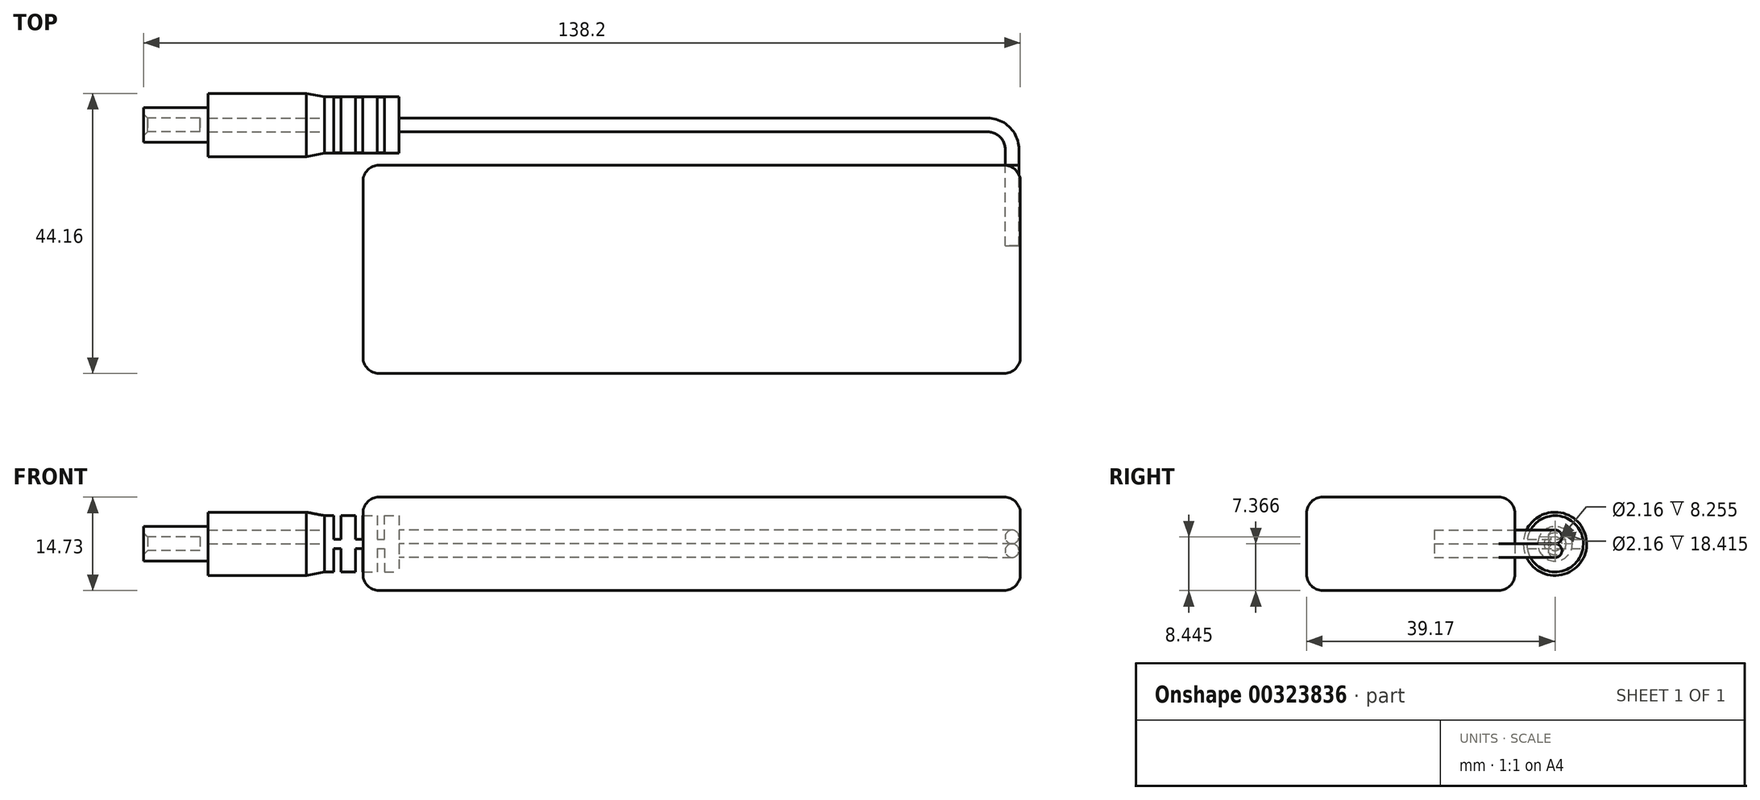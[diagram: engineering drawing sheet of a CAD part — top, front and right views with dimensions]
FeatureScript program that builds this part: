
annotation { "Feature Type Name" : "Feature", "Feature Type Description" : "" }
export const myFeature = defineFeature(function(context is Context, id is Id, definition is map)
    precondition{}
    {
        {
            var Q0;
            Q0=qCreatedBy(makeId("Top.planeOp"),FACE);
            var sketch = newSketch(context, id + "F0", { "sketchPlane" : qUnion([Q0])});
            skLineSegment(sketch, "E0.bottom", {"start": v(0, 0) * mm, "end": v(103.62, 0) * mm});
            skLineSegment(sketch, "E0.top", {"start": v(0, -32.82) * mm, "end": v(103.62, -32.82) * mm});
            skLineSegment(sketch, "E0.left", {"start": v(0, 0) * mm, "end": v(0, -32.82) * mm});
            skLineSegment(sketch, "E0.right", {"start": v(103.62, 0) * mm, "end": v(103.62, -32.82) * mm});
            skSolve(sketch);
        }
        {
            var Q0;
            Q0=makeQuery(id+"F0.imprint","IMPRINT",FACE,{"disambiguationData":[TD([[makeQuery(id+"F0.imprint","IMPRINT",EDGE,{"derivedFrom":sQuery(id+"F0.wireOp",EDGE,"E0.bottom")}),-1.0]])]});
            extrude(context, id + "F1", {"entities" : qUnion([Q0]), "depth" : 14.73 * mm});
        }
        {
            var Q0;
            Q0=makeQuery(id+"F1.opExtrude","CAP_EDGE",EDGE,{"disambiguationData":[OSD([sQuery(id+"F0.wireOp",EDGE,"E0.top")])],"isStart":false});
            var Q1;
            Q1=makeQuery(id+"F1.opExtrude","CAP_FACE",FACE,{"disambiguationData":[OSD([sQuery(id+"F0.wireOp",EDGE,"E0.bottom"),sQuery(id+"F0.wireOp",EDGE,"E0.top"),sQuery(id+"F0.wireOp",EDGE,"E0.left"),sQuery(id+"F0.wireOp",EDGE,"E0.right")])],"isStart":false});
            var Q2;
            Q2=makeQuery(id+"F1.opExtrude","SWEPT_EDGE",EDGE,{"disambiguationData":[OSD([sQuery(id+"F0.wireOp",EDGE,"E0.top"),sQuery(id+"F0.wireOp",EDGE,"E0.right")])]});
            var Q3;
            Q3=makeQuery(id+"F1.opExtrude","SWEPT_EDGE",EDGE,{"disambiguationData":[OSD([sQuery(id+"F0.wireOp",EDGE,"E0.bottom"),sQuery(id+"F0.wireOp",EDGE,"E0.right")])]});
            var Q4;
            Q4=makeQuery(id+"F1.opExtrude","CAP_EDGE",EDGE,{"disambiguationData":[OSD([sQuery(id+"F0.wireOp",EDGE,"E0.right")])],"isStart":true});
            var Q5;
            Q5=makeQuery(id+"F1.opExtrude","CAP_FACE",FACE,{"disambiguationData":[OSD([sQuery(id+"F0.wireOp",EDGE,"E0.bottom"),sQuery(id+"F0.wireOp",EDGE,"E0.top"),sQuery(id+"F0.wireOp",EDGE,"E0.left"),sQuery(id+"F0.wireOp",EDGE,"E0.right")])],"isStart":true});
            var Q6;
            Q6=makeQuery(id+"F1.opExtrude","SWEPT_FACE",FACE,{"disambiguationData":[OSD([sQuery(id+"F0.wireOp",EDGE,"E0.left")])]});
            var Q7;
            Q7=makeQuery(id+"F1.opExtrude","SWEPT_FACE",FACE,{"disambiguationData":[OSD([sQuery(id+"F0.wireOp",EDGE,"E0.top")])]});
            fillet(context, id + "F2", {"entities" : qUnion([Q0, Q1, Q2, Q3, Q4, Q5, Q6, Q7]), "radius" : 2.54 * mm, "tangentPropagation" : true, "allowEdgeOverflow" : false});
        }
        {
            var Q0;
            Q0=makeQuery(id+"F1.opExtrude","SWEPT_FACE",FACE,{"disambiguationData":[OSD([sQuery(id+"F0.wireOp",EDGE,"E0.bottom")])]});
            var sketch = newSketch(context, id + "F3", { "sketchPlane" : qUnion([Q0])});
            skCircle(sketch, "E1", {"center": v(-102.3, 6.29) * mm, "radius": 1.08 * mm});
            skCircle(sketch, "E2", {"center": v(-102.3, 8.45) * mm, "radius": 1.08 * mm});
            skSolve(sketch);
        }
        {
            var Q0;
            Q0=makeQuery(id+"F3.imprint","IMPRINT",FACE,{"disambiguationData":[TD([[makeQuery(id+"F3.imprint","IMPRINT",EDGE,{"derivedFrom":sQuery(id+"F3.wireOp",EDGE,"E1")}),1.0]])]});
            var Q1;
            Q1=makeQuery(id+"F3.imprint","IMPRINT",FACE,{"disambiguationData":[TD([[makeQuery(id+"F3.imprint","IMPRINT",EDGE,{"derivedFrom":sQuery(id+"F3.wireOp",EDGE,"E2")}),1.0]])]});
            extrude(context, id + "F4", {"entities" : qUnion([Q0, Q1]), "oppositeDirection" : true, "depth" : 12.7 * mm});
        }
        {
            var Q0;
            Q0=makeQuery(id+"F1.opExtrude","CAP_FACE",FACE,{"disambiguationData":[OSD([sQuery(id+"F0.wireOp",EDGE,"E0.bottom"),sQuery(id+"F0.wireOp",EDGE,"E0.top"),sQuery(id+"F0.wireOp",EDGE,"E0.left"),sQuery(id+"F0.wireOp",EDGE,"E0.right")])],"isStart":true});
            cPlane(context, id + "F5", {"entities" : qUnion([Q0]), "cplaneType" : CPlaneType.OFFSET, "offset" : 6.25 * mm, "oppositeDirection" : true, "width" : 152.4 * mm, "height" : 152.4 * mm});
        }
        {
            var Q0;
            Q0=qCreatedBy(id+"F5.planeOp",FACE);
            cPlane(context, id + "F6", {"entities" : qUnion([Q0]), "cplaneType" : CPlaneType.OFFSET, "offset" : 2.18 * mm, "oppositeDirection" : true, "width" : 152.4 * mm, "height" : 152.4 * mm});
        }
        {
            var Q0;
            Q0=qCreatedBy(id+"F5.planeOp",FACE);
            var sketch = newSketch(context, id + "F7", { "sketchPlane" : qUnion([Q0])});
            skPoint(sketch, "E3.endSnap0", {"position": v(102.3, 0) * mm});
            skLineSegment(sketch, "E4", {"start": v(102.3, 0) * mm, "end": v(102.3, -2.54) * mm});
            skLineSegment(sketch, "E5", {"start": v(98.5, -6.35) * mm, "end": v(5.66, -6.35) * mm});
            skPoint(sketch, "E6.visualSharp", {"position": v(102.3, -6.35) * mm});
            skArc(sketch, "E6.filletArc", {"start": v(98.5, -6.35) * mm, "mid": v(101.2, -5.23) * mm, "end": v(102.3, -2.54) * mm});
            skSolve(sketch);
        }
        {
            var Q0;
            Q0=qCreatedBy(id+"F6.planeOp",FACE);
            var sketch = newSketch(context, id + "F8", { "sketchPlane" : qUnion([Q0])});
            skLineSegment(sketch, "E7.0", {"start": v(102.3, 0) * mm, "end": v(102.3, -2.54) * mm});
            skArc(sketch, "E8.0", {"start": v(98.5, -6.35) * mm, "mid": v(101.2, -5.23) * mm, "end": v(102.3, -2.54) * mm});
            skLineSegment(sketch, "E9.0", {"start": v(98.5, -6.35) * mm, "end": v(5.66, -6.35) * mm});
            skSolve(sketch);
        }
        {
            var Q0;
            Q0=makeQuery(id+"F4.opExtrude","CAP_FACE",FACE,{"disambiguationData":[OSD([sQuery(id+"F3.wireOp",EDGE,"E1")])],"isStart":true});
            var Q1;
            Q1=sQuery(id+"F7.wireOp",EDGE,"E4");
            var Q2;
            Q2=sQuery(id+"F7.wireOp",EDGE,"E6.filletArc");
            var Q3;
            Q3=sQuery(id+"F7.wireOp",EDGE,"E5");
            sweep(context, id + "F9", {"operationType" : NewBodyOperationType.ADD, "profiles" : qUnion([Q0]), "path" : qUnion([Q1, Q2, Q3])});
        }
        {
            var Q0;
            Q0=makeQuery(id+"F4.opExtrude","CAP_FACE",FACE,{"disambiguationData":[OSD([sQuery(id+"F3.wireOp",EDGE,"E2")])],"isStart":true});
            var Q1;
            Q1=sQuery(id+"F8.wireOp",EDGE,"E7.0");
            var Q2;
            Q2=sQuery(id+"F8.wireOp",EDGE,"E8.0");
            var Q3;
            Q3=sQuery(id+"F8.wireOp",EDGE,"E9.0");
            sweep(context, id + "F10", {"profiles" : qUnion([Q0]), "path" : qUnion([Q1, Q2, Q3])});
        }
        {
            var Q0;
            Q0=makeQuery(id+"F10.opSweep","CAP_FACE",FACE,{"disambiguationData":[OSD([sQuery(id+"F3.wireOp",EDGE,"E2"),sQuery(id+"F8.wireOp",VERTEX,"E9.0.end")])],"isStart":false});
            var sketch = newSketch(context, id + "F11", { "sketchPlane" : qUnion([Q0])});
            skSolve(sketch);
        }
        {
            var Q0;
            Q0=makeQuery(id+"F9.opSweep","CAP_FACE",FACE,{"disambiguationData":[OSD([sQuery(id+"F3.wireOp",EDGE,"E1"),sQuery(id+"F7.wireOp",VERTEX,"E5.end")])],"isStart":false});
            var sketch = newSketch(context, id + "F12", { "sketchPlane" : qUnion([Q0])});
            skCircle(sketch, "E10.0", {"center": v(-6.35, 6.29) * mm, "radius": 1.08 * mm});
            skCircle(sketch, "E11.0", {"center": v(-6.35, 8.45) * mm, "radius": 1.08 * mm});
            skCircle(sketch, "E12", {"center": v(-6.35, 7.37) * mm, "radius": 4.45 * mm});
            skSolve(sketch);
        }
        {
            var Q0;
            Q0=makeQuery(id+"F12.imprint","IMPRINT",FACE,{"disambiguationData":[TD([[makeQuery(id+"F12.imprint","IMPRINT",EDGE,{"derivedFrom":sQuery(id+"F12.wireOp",EDGE,"E10.0")}),-1.0]])]});
            var Q1;
            Q1=makeQuery(id+"F12.imprint","IMPRINT",FACE,{"disambiguationData":[TD([[makeQuery(id+"F12.imprint","IMPRINT",EDGE,{"derivedFrom":sQuery(id+"F12.wireOp",EDGE,"E10.0")}),1.0]])]});
            var Q2;
            Q2=makeQuery(id+"F11.imprint","IMPRINT",FACE,{"disambiguationData":[TD([[makeQuery(id+"F11.imprint","IMPRINT",EDGE,{"derivedFrom":makeQuery(id+"F10.opSweep","CAP_EDGE",EDGE,{"disambiguationData":[OSD([sQuery(id+"F3.wireOp",EDGE,"E2"),sQuery(id+"F8.wireOp",VERTEX,"E9.0.end")])],"isStart":false})}),1.0]])]});
            extrude(context, id + "F13", {"entities" : qUnion([Q0, Q1, Q2]), "depth" : 11.67 * mm});
        }
        {
            var Q0;
            Q0=makeQuery(id+"F1.opExtrude","SWEPT_FACE",FACE,{"disambiguationData":[OSD([sQuery(id+"F0.wireOp",EDGE,"E0.bottom")])]});
            cPlane(context, id + "F14", {"entities" : qUnion([Q0]), "cplaneType" : CPlaneType.OFFSET, "offset" : 25.4 * mm, "width" : 152.4 * mm, "height" : 152.4 * mm});
        }
        {
            var Q0;
            Q0=qCreatedBy(id+"F14.planeOp",FACE);
            var sketch = newSketch(context, id + "F15", { "sketchPlane" : qUnion([Q0])});
            skLineSegment(sketch, "E13", {"start": v(-5.66, 11.81) * mm, "end": v(6, 11.81) * mm});
            skLineSegment(sketch, "E14", {"start": v(6, 2.92) * mm, "end": v(-5.66, 2.92) * mm});
            skLineSegment(sketch, "E15.0", {"start": v(-5.66, 11.81) * mm, "end": v(-5.66, 2.92) * mm});
            skLineSegment(sketch, "E16.0", {"start": v(6, 11.81) * mm, "end": v(6, 2.92) * mm});
            skLineSegment(sketch, "E17", {"start": v(-3.38, 0.86) * mm, "end": v(-3.38, 6.63) * mm});
            skLineSegment(sketch, "E18", {"start": v(-3.38, 6.63) * mm, "end": v(-2.23, 6.63) * mm});
            skLineSegment(sketch, "E19", {"start": v(-2.23, 6.63) * mm, "end": v(-2.23, 0.86) * mm});
            skLineSegment(sketch, "E20", {"start": v(0.05, 0.86) * mm, "end": v(0.05, 6.63) * mm});
            skLineSegment(sketch, "E21", {"start": v(0.05, 6.63) * mm, "end": v(1.2, 6.63) * mm});
            skLineSegment(sketch, "E22", {"start": v(1.2, 6.63) * mm, "end": v(1.2, 0.86) * mm});
            skLineSegment(sketch, "E23", {"start": v(3.48, 0.86) * mm, "end": v(3.48, 6.63) * mm});
            skLineSegment(sketch, "E24", {"start": v(3.48, 6.63) * mm, "end": v(4.62, 6.63) * mm});
            skLineSegment(sketch, "E25", {"start": v(4.62, 6.63) * mm, "end": v(4.62, 0.86) * mm});
            skLineSegment(sketch, "E26", {"start": v(6, 7.37) * mm, "end": v(-5.66, 7.37) * mm, "construction": true});
            skLineSegment(sketch, "E27", {"start": v(8.74, 0.86) * mm, "end": v(-3.38, 0.86) * mm, "construction": true});
            skPoint(sketch, "E28.orphan", {"position": v(4.62, 2.92) * mm});
            skPoint(sketch, "E29.orphan", {"position": v(3.48, 2.92) * mm});
            skPoint(sketch, "E30.orphan", {"position": v(1.2, 2.92) * mm});
            skPoint(sketch, "E31.orphan", {"position": v(0.05, 2.92) * mm});
            skPoint(sketch, "E32.orphan", {"position": v(-2.23, 2.92) * mm});
            skPoint(sketch, "E33.orphan", {"position": v(-3.38, 2.92) * mm});
            skLineSegment(sketch, "E34.MirrorCS", {"start": v(-3.38, 13.87) * mm, "end": v(-3.38, 8.1) * mm});
            skLineSegment(sketch, "E35.MirrorCS", {"start": v(-3.38, 8.1) * mm, "end": v(-2.23, 8.1) * mm});
            skLineSegment(sketch, "E36.MirrorCS", {"start": v(-2.23, 8.1) * mm, "end": v(-2.23, 13.87) * mm});
            skLineSegment(sketch, "E37.MirrorCS", {"start": v(0.05, 13.87) * mm, "end": v(0.05, 8.1) * mm});
            skLineSegment(sketch, "E38.MirrorCS", {"start": v(0.05, 8.1) * mm, "end": v(1.2, 8.1) * mm});
            skLineSegment(sketch, "E39.MirrorCS", {"start": v(1.2, 8.1) * mm, "end": v(1.2, 13.87) * mm});
            skLineSegment(sketch, "E40.MirrorCS", {"start": v(3.48, 13.87) * mm, "end": v(3.48, 8.1) * mm});
            skLineSegment(sketch, "E41.MirrorCS", {"start": v(3.48, 8.1) * mm, "end": v(4.62, 8.1) * mm});
            skLineSegment(sketch, "E42.MirrorCS", {"start": v(4.62, 8.1) * mm, "end": v(4.62, 13.87) * mm});
            skLineSegment(sketch, "E43", {"start": v(4.62, 0.86) * mm, "end": v(-3.38, 0.86) * mm});
            skLineSegment(sketch, "E44", {"start": v(4.62, 13.87) * mm, "end": v(-3.38, 13.87) * mm});
            skSolve(sketch);
        }
        {
            var Q0;
            {var subQ0=sQuery(id+"F15.wireOp",EDGE,"E25");var subQ1=sQuery(id+"F15.wireOp",EDGE,"E14");var subQ2=makeQuery(id+"F15.imprint","INTERSECT",VERTEX,{"derivedFrom":[subQ1,subQ0]});Q0=makeQuery(id+"F15.imprint","IMPRINT",FACE,{"disambiguationData":[TD([[makeQuery(id+"F15.imprint","IMPRINT",EDGE,{"disambiguationData":[TD([[subQ2,-1.0]])],"derivedFrom":subQ1}),1.0]])]});}
            var Q1;
            {var subQ5=sQuery(id+"F15.wireOp",EDGE,"E24");Q1=makeQuery(id+"F15.imprint","IMPRINT",FACE,{"disambiguationData":[TD([[makeQuery(id+"F15.imprint","IMPRINT",EDGE,{"derivedFrom":subQ5}),-1.0]])]});}
            var Q2;
            {var subQ0=sQuery(id+"F15.wireOp",EDGE,"E22");var subQ1=sQuery(id+"F15.wireOp",EDGE,"E14");var subQ2=makeQuery(id+"F15.imprint","INTERSECT",VERTEX,{"derivedFrom":[subQ1,subQ0]});Q2=makeQuery(id+"F15.imprint","IMPRINT",FACE,{"disambiguationData":[TD([[makeQuery(id+"F15.imprint","IMPRINT",EDGE,{"disambiguationData":[TD([[subQ2,-1.0]])],"derivedFrom":subQ1}),1.0]])]});}
            var Q3;
            {var subQ5=sQuery(id+"F15.wireOp",EDGE,"E21");Q3=makeQuery(id+"F15.imprint","IMPRINT",FACE,{"disambiguationData":[TD([[makeQuery(id+"F15.imprint","IMPRINT",EDGE,{"derivedFrom":subQ5}),-1.0]])]});}
            var Q4;
            {var subQ0=sQuery(id+"F15.wireOp",EDGE,"E17");var subQ1=sQuery(id+"F15.wireOp",EDGE,"E14");var subQ2=makeQuery(id+"F15.imprint","INTERSECT",VERTEX,{"derivedFrom":[subQ1,subQ0]});Q4=makeQuery(id+"F15.imprint","IMPRINT",FACE,{"disambiguationData":[TD([[makeQuery(id+"F15.imprint","IMPRINT",EDGE,{"disambiguationData":[TD([[subQ2,1.0]])],"derivedFrom":subQ1}),1.0]])]});}
            var Q5;
            {var subQ5=sQuery(id+"F15.wireOp",EDGE,"E18");Q5=makeQuery(id+"F15.imprint","IMPRINT",FACE,{"disambiguationData":[TD([[makeQuery(id+"F15.imprint","IMPRINT",EDGE,{"derivedFrom":subQ5}),-1.0]])]});}
            var Q6;
            {var subQ5=sQuery(id+"F15.wireOp",EDGE,"E35.MirrorCS");Q6=makeQuery(id+"F15.imprint","IMPRINT",FACE,{"disambiguationData":[TD([[makeQuery(id+"F15.imprint","IMPRINT",EDGE,{"derivedFrom":subQ5}),1.0]])]});}
            var Q7;
            {var subQ5=sQuery(id+"F15.wireOp",EDGE,"E38.MirrorCS");Q7=makeQuery(id+"F15.imprint","IMPRINT",FACE,{"disambiguationData":[TD([[makeQuery(id+"F15.imprint","IMPRINT",EDGE,{"derivedFrom":subQ5}),1.0]])]});}
            var Q8;
            {var subQ0=sQuery(id+"F15.wireOp",EDGE,"E34.MirrorCS");var subQ1=sQuery(id+"F15.wireOp",EDGE,"E13");var subQ2=makeQuery(id+"F15.imprint","INTERSECT",VERTEX,{"derivedFrom":[subQ1,subQ0]});Q8=makeQuery(id+"F15.imprint","IMPRINT",FACE,{"disambiguationData":[TD([[makeQuery(id+"F15.imprint","IMPRINT",EDGE,{"disambiguationData":[TD([[subQ2,-1.0]])],"derivedFrom":subQ1}),1.0]])]});}
            var Q9;
            {var subQ0=sQuery(id+"F15.wireOp",EDGE,"E37.MirrorCS");var subQ1=sQuery(id+"F15.wireOp",EDGE,"E13");var subQ2=makeQuery(id+"F15.imprint","INTERSECT",VERTEX,{"derivedFrom":[subQ1,subQ0]});Q9=makeQuery(id+"F15.imprint","IMPRINT",FACE,{"disambiguationData":[TD([[makeQuery(id+"F15.imprint","IMPRINT",EDGE,{"disambiguationData":[TD([[subQ2,-1.0]])],"derivedFrom":subQ1}),1.0]])]});}
            var Q10;
            {var subQ0=sQuery(id+"F15.wireOp",EDGE,"E42.MirrorCS");var subQ1=sQuery(id+"F15.wireOp",EDGE,"E13");var subQ2=makeQuery(id+"F15.imprint","INTERSECT",VERTEX,{"derivedFrom":[subQ1,subQ0]});Q10=makeQuery(id+"F15.imprint","IMPRINT",FACE,{"disambiguationData":[TD([[makeQuery(id+"F15.imprint","IMPRINT",EDGE,{"disambiguationData":[TD([[subQ2,1.0]])],"derivedFrom":subQ1}),1.0]])]});}
            var Q11;
            {var subQ5=sQuery(id+"F15.wireOp",EDGE,"E41.MirrorCS");Q11=makeQuery(id+"F15.imprint","IMPRINT",FACE,{"disambiguationData":[TD([[makeQuery(id+"F15.imprint","IMPRINT",EDGE,{"derivedFrom":subQ5}),1.0]])]});}
            extrude(context, id + "F16", {"entities" : qUnion([Q0, Q1, Q2, Q3, Q4, Q5, Q6, Q7, Q8, Q9, Q10, Q11]), "operationType" : NewBodyOperationType.REMOVE, "oppositeDirection" : true, "depth" : 24.13 * mm});
        }
        {
            var Q0;
            Q0=makeQuery(id+"F13.boolean.opBoolean","MERGE",FACE,{"derivedFrom":[makeQuery(id+"F13.opExtrude","CAP_FACE",FACE,{"disambiguationData":[OSD([sQuery(id+"F3.wireOp",EDGE,"E2"),sQuery(id+"F8.wireOp",VERTEX,"E9.0.end")])],"isStart":false}),makeQuery(id+"F13.opExtrude","CAP_FACE",FACE,{"disambiguationData":[OSD([sQuery(id+"F12.wireOp",EDGE,"E11.0"),sQuery(id+"F12.wireOp",EDGE,"E12")])],"isStart":false})]});
            var sketch = newSketch(context, id + "F17", { "sketchPlane" : qUnion([Q0])});
            skCircle(sketch, "E45.0.0", {"center": v(-6.35, 7.37) * mm, "radius": 4.45 * mm});
            skCircle(sketch, "E46", {"center": v(-6.35, 7.37) * mm, "radius": 5 * mm});
            skSolve(sketch);
        }
        {
            var Q0;
            Q0=makeQuery(id+"F17.imprint","IMPRINT",FACE,{"disambiguationData":[TD([[makeQuery(id+"F17.imprint","IMPRINT",EDGE,{"derivedFrom":sQuery(id+"F17.wireOp",EDGE,"E45.0.0")}),-1.0]])]});
            var Q1;
            Q1=makeQuery(id+"F17.imprint","IMPRINT",FACE,{"disambiguationData":[TD([[makeQuery(id+"F17.imprint","IMPRINT",EDGE,{"derivedFrom":sQuery(id+"F17.wireOp",EDGE,"E45.0.0")}),1.0]])]});
            extrude(context, id + "F18", {"entities" : qUnion([Q0, Q1]), "operationType" : NewBodyOperationType.ADD, "depth" : 18.41 * mm});
        }
        {
            var Q0;
            Q0=makeQuery(id+"F18.opExtrude","CAP_EDGE",EDGE,{"disambiguationData":[OSD([sQuery(id+"F17.wireOp",EDGE,"E46")])],"isStart":true});
            chamfer(context, id + "F19", {"entities" : qUnion([Q0]), "chamferType" : ChamferType.TWO_OFFSETS, "width1" : 2.92 * mm, "oppositeDirection" : false, "width2" : 0.56 * mm, "tangentPropagation" : true});
        }
        {
            var Q0;
            Q0=makeQuery(id+"F18.opExtrude","CAP_FACE",FACE,{"disambiguationData":[OSD([sQuery(id+"F17.wireOp",EDGE,"E46")])],"isStart":false});
            cPlane(context, id + "F20", {"entities" : qUnion([Q0]), "cplaneType" : CPlaneType.OFFSET, "offset" : 1.27 * mm, "width" : 152.4 * mm, "height" : 152.4 * mm});
        }
        {
            var Q0;
            Q0=qCreatedBy(id+"F20.planeOp",FACE);
            var sketch = newSketch(context, id + "F21", { "sketchPlane" : qUnion([Q0])});
            skCircle(sketch, "E47", {"center": v(-6.35, 7.37) * mm, "radius": 2.72 * mm});
            skSolve(sketch);
        }
        {
            var Q0;
            Q0=makeQuery(id+"F21.imprint","IMPRINT",FACE,{"disambiguationData":[TD([[makeQuery(id+"F21.imprint","IMPRINT",EDGE,{"derivedFrom":sQuery(id+"F21.wireOp",EDGE,"E47")}),1.0]])]});
            var Q1;
            Q1=makeQuery(id+"F18.opExtrude","CAP_FACE",FACE,{"disambiguationData":[OSD([sQuery(id+"F17.wireOp",EDGE,"E46")])],"isStart":false});
            extrude(context, id + "F22", {"entities" : qUnion([Q0]), "endBound" : BoundingType.UP_TO_SURFACE, "oppositeDirection" : true, "endBoundEntityFace" : qUnion([Q1]), "depth" : 2.54 * mm});
        }
        {
            var Q0;
            Q0=makeQuery(id+"F22.opExtrude","CAP_FACE",FACE,{"disambiguationData":[OSD([sQuery(id+"F21.wireOp",EDGE,"E47")])],"isStart":true});
            extrude(context, id + "F23", {"entities" : qUnion([Q0]), "operationType" : NewBodyOperationType.ADD, "depth" : 8.9 * mm});
        }
        {
            var Q0;
            Q0=makeQuery(id+"F23.opExtrude","CAP_FACE",FACE,{"disambiguationData":[OSD([sQuery(id+"F21.wireOp",EDGE,"E47")])],"isStart":false});
            var sketch = newSketch(context, id + "F24", { "sketchPlane" : qUnion([Q0])});
            skCircle(sketch, "E48", {"center": v(-6.35, 7.37) * mm, "radius": 1.08 * mm});
            skSolve(sketch);
        }
        {
            var Q0;
            Q0 = qSketchRegion(id + "F24", true);
            extrude(context, id + "F25", {"entities" : qUnion([Q0]), "operationType" : NewBodyOperationType.REMOVE, "endBound" : BoundingType.SYMMETRIC, "oppositeDirection" : true, "depth" : 17.78 * mm});
        }
        {
            var Q0;
            Q0=makeQuery(id+"F25.boolean.opBoolean","INTERSECT",EDGE,{"derivedFrom":[makeQuery(id+"F23.opExtrude","CAP_FACE",FACE,{"disambiguationData":[OSD([sQuery(id+"F21.wireOp",EDGE,"E47")])],"isStart":false}),makeQuery(id+"F25.opExtrude","SWEPT_FACE",FACE,{"disambiguationData":[OSD([sQuery(id+"F24.wireOp",EDGE,"E48")])]})]});
            chamfer(context, id + "F26", {"entities" : qUnion([Q0]), "width" : 0.64 * mm, "tangentPropagation" : true});
        }
    });
